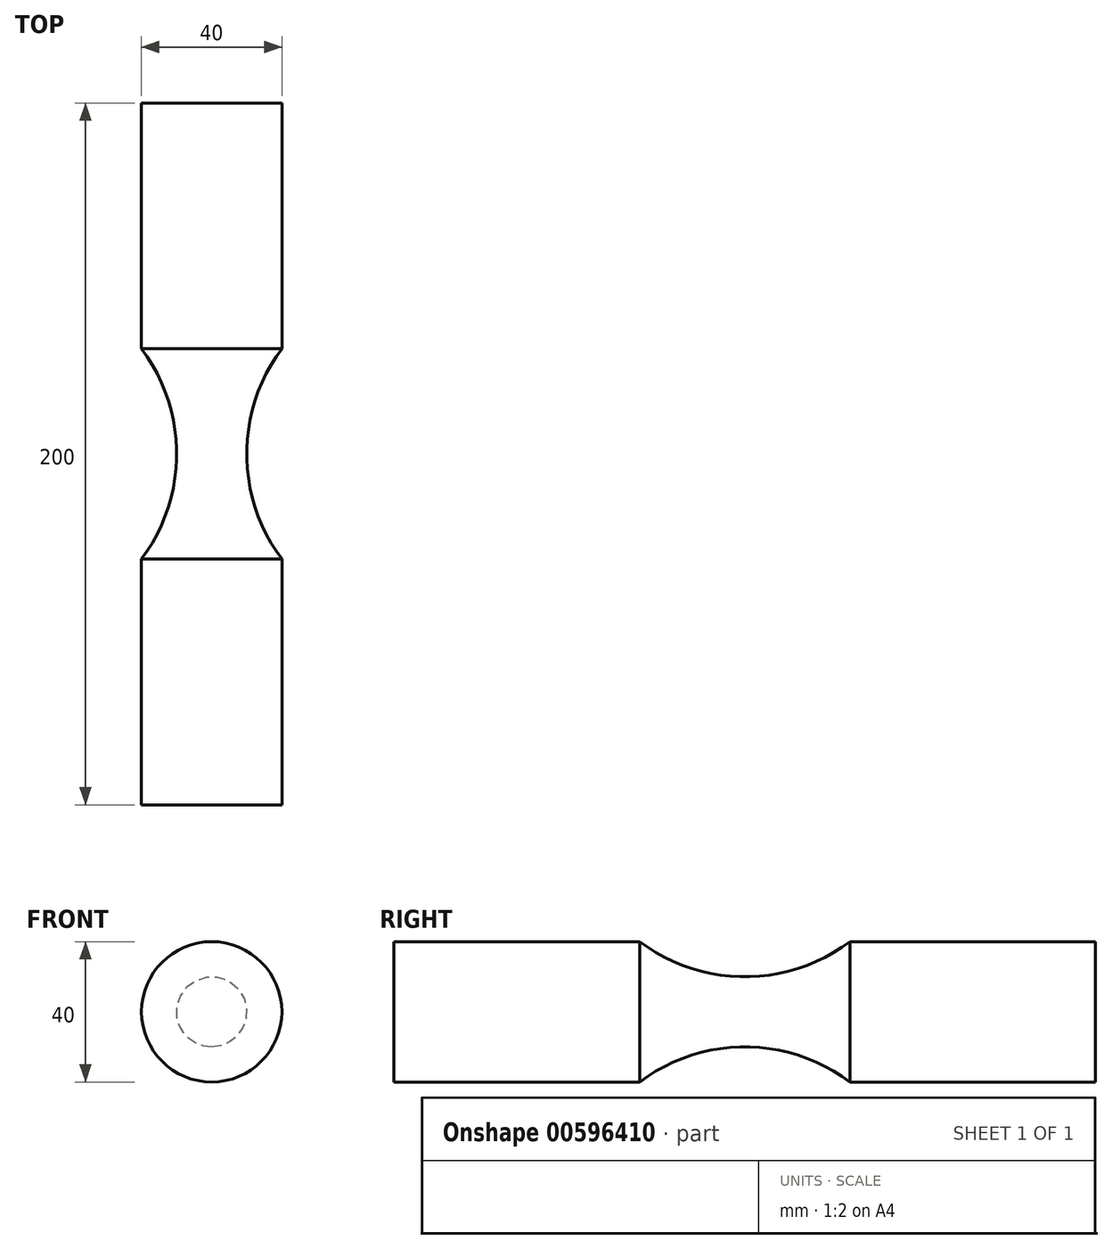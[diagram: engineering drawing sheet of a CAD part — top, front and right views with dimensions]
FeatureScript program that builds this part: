
annotation { "Feature Type Name" : "Feature", "Feature Type Description" : "" }
export const myFeature = defineFeature(function(context is Context, id is Id, definition is map)
    precondition{}
    {
        {
            var Q0;
            Q0=qCreatedBy(makeId("Right.planeOp"),FACE);
            var sketch = newSketch(context, id + "F0", { "sketchPlane" : qUnion([Q0])});
            skLineSegment(sketch, "E0", {"start": v(-100, 20) * mm, "end": v(-100, 0) * mm});
            skLineSegment(sketch, "E1", {"start": v(-100, 0) * mm, "end": v(0, 0) * mm});
            skLineSegment(sketch, "E2", {"start": v(0, 0) * mm, "end": v(0, 10) * mm});
            skLineSegment(sketch, "E3", {"start": v(-100, 20) * mm, "end": v(-30, 20) * mm});
            skArc(sketch, "E4", {"start": v(-30, 20) * mm, "mid": v(-15.81, 12.57) * mm, "end": v(0, 10) * mm});
            skLineSegment(sketch, "E5", {"start": v(0, 10) * mm, "end": v(31.02, 10) * mm});
            skSolve(sketch);
        }
        {
            var Q0;
            Q0=makeQuery(id+"F0.imprint","IMPRINT",FACE,{"disambiguationData":[TD([[makeQuery(id+"F0.imprint","IMPRINT",EDGE,{"derivedFrom":sQuery(id+"F0.wireOp",EDGE,"E0")}),1.0]])]});
            var Q1;
            Q1=sQuery(id+"F0.wireOp",EDGE,"E1");
            revolve(context, id + "F1", {"entities" : qUnion([Q0]), "axis" : qUnion([Q1]), "revolveType" : RevolveType.FULL});
        }
        {
            var Q0;
            Q0=makeQuery(id+"F1.opRevolve","SWEPT_BODY",BODY,{"disambiguationData":[OSD([sQuery(id+"F0.wireOp",EDGE,"E0"),sQuery(id+"F0.wireOp",EDGE,"E1"),sQuery(id+"F0.wireOp",EDGE,"E2"),sQuery(id+"F0.wireOp",EDGE,"E3"),sQuery(id+"F0.wireOp",EDGE,"E4")])]});
            var Q1;
            Q1=qCreatedBy(makeId("Front.planeOp"),FACE);
            mirror(context, id + "F2", {"operationType" : NewBodyOperationType.ADD, "entities" : qUnion([Q0]), "mirrorPlane" : qUnion([Q1])});
        }
    });
